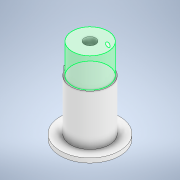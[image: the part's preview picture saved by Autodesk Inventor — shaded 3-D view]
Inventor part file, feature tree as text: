
AUTODESK INVENTOR PART (.ipt)
format: ipt  version: 2020 (Build 240168000, 168)  size: 150,016 bytes
history: native  units: mm
features: sketch x5, extrude x4, hole x1
ambient origin geometry x8: Origin, YZ Plane, XZ Plane, XY Plane, X Axis, Y Axis, Z Axis, Center Point
bodies: Solid1 (feature_tree)
feature tree (10):
  extrude  "Extrusion1"  Depth=17.0mm TaperAngle=0.0deg
  extrude  "Extrusion2"  Depth=1.5mm TaperAngle=0.0deg
  extrude  "Extrusion3"  Depth=3.0mm
  hole  "Hole1"  [1 undecoded]
  extrude  "Extrusion4"  Depth=10.0mm
  sketch  "Sketch1"  dims[d0=13.0mm d1=17.0mm d2=0.0mm]
  sketch  "Sketch2"  dims[d3=20.0mm d4=1.5mm d5=0.0mm]
  sketch  "Sketch4"  dims[d8=1.0mm d9=3.0mm]
  sketch  "Sketch5"  dims[d10=12.0mm d11=10.0mm d12=0.0mm]
  sketch  "Sketch6"  dims[d13=3.8mm d14=6.0mm d15=11.0mm d16=2.6mm d17=90.0deg d18=10.0mm d19=20.594885mm d21=1.5mm d24=10.0mm d25=0.0mm d26=4.0mm]
note: 1 required parameter value undecoded (feature->parameter linkage not recoverable at this tier; creation-order binding heuristic only, values carry confidence <= 0.55)
